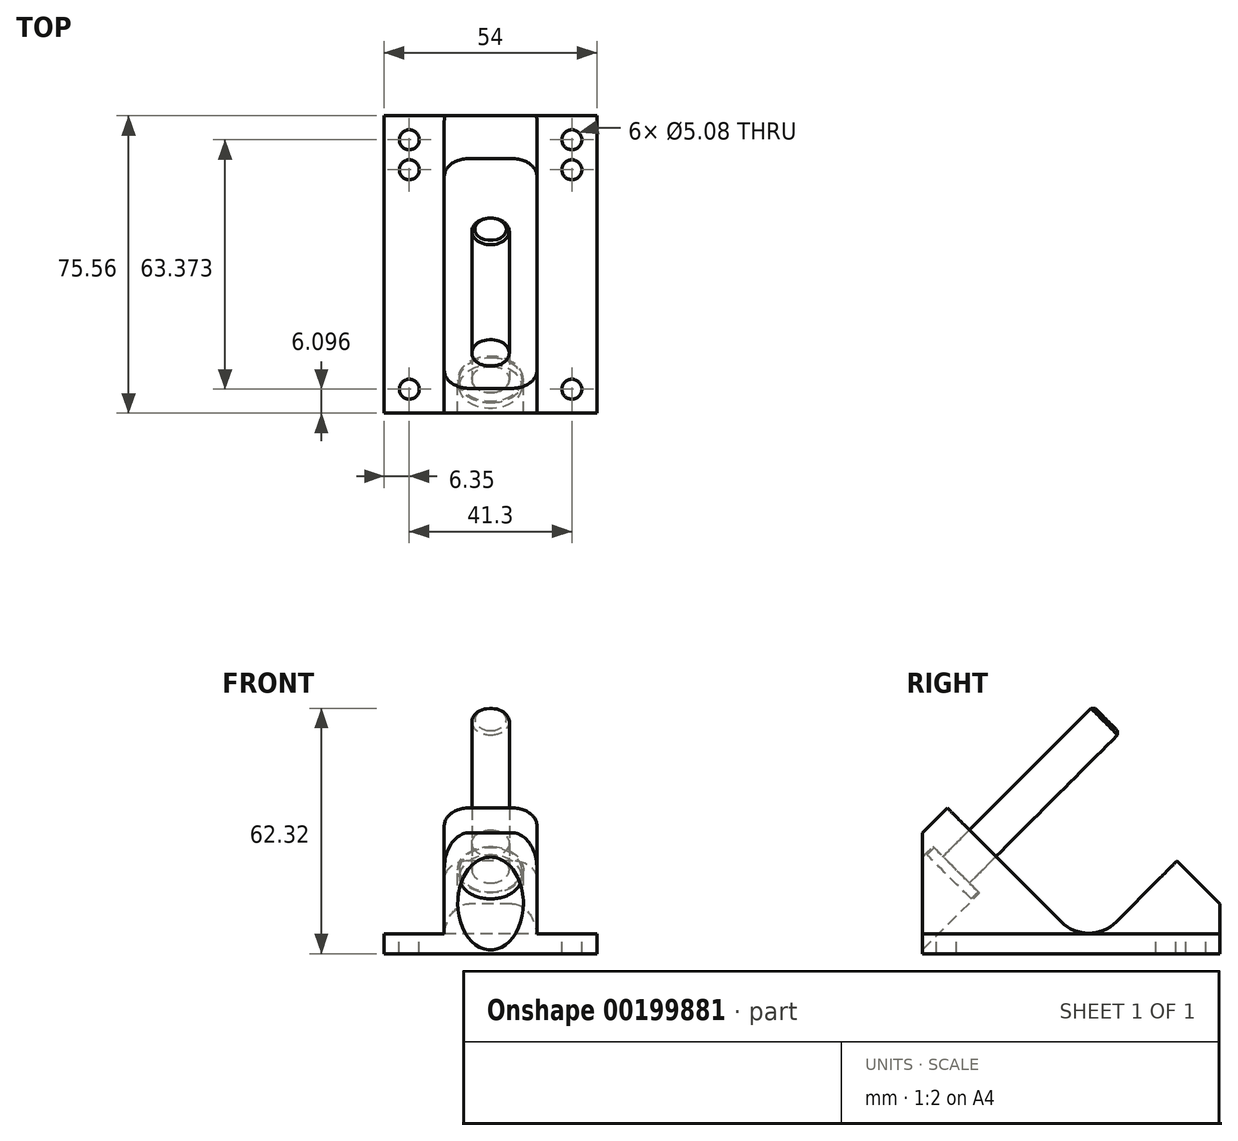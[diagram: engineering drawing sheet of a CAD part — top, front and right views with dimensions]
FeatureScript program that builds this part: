
annotation { "Feature Type Name" : "Feature", "Feature Type Description" : "" }
export const myFeature = defineFeature(function(context is Context, id is Id, definition is map)
    precondition{}
    {
        {
            var Q0;
            Q0=qCreatedBy(makeId("Right.planeOp"),FACE);
            var sketch = newSketch(context, id + "F0", { "sketchPlane" : qUnion([Q0])});
            skLineSegment(sketch, "E0", {"start": v(0, 0) * mm, "end": v(0, 30.72) * mm});
            skLineSegment(sketch, "E1", {"start": v(0, 30.72) * mm, "end": v(6.32, 37.04) * mm});
            skLineSegment(sketch, "E2", {"start": v(6.32, 37.04) * mm, "end": v(42.25, 1.12) * mm});
            skLineSegment(sketch, "E3", {"start": v(42.25, 1.12) * mm, "end": v(64.7, 23.57) * mm});
            skLineSegment(sketch, "E4", {"start": v(64.7, 23.57) * mm, "end": v(75.57, 12.7) * mm});
            skLineSegment(sketch, "E5", {"start": v(75.57, 12.7) * mm, "end": v(75.57, 0) * mm});
            skLineSegment(sketch, "E6", {"start": v(75.57, 0) * mm, "end": v(0, 0) * mm});
            skLineSegment(sketch, "E7", {"start": v(15.3, 28.06) * mm, "end": v(28.77, 41.53) * mm, "construction": true});
            skLineSegment(sketch, "E8", {"start": v(28.77, 41.53) * mm, "end": v(55.72, 14.59) * mm, "construction": true});
            skLineSegment(sketch, "E9", {"start": v(55.72, 14.59) * mm, "end": v(64.7, 5.6) * mm, "construction": true});
            skLineSegment(sketch, "E10", {"start": v(64.7, 5.6) * mm, "end": v(70.08, 11) * mm, "construction": true});
            skLineSegment(sketch, "E11", {"start": v(70.08, 11) * mm, "end": v(61.1, 19.98) * mm, "construction": true});
            skLineSegment(sketch, "E12", {"start": v(28.77, 41.53) * mm, "end": v(15.3, 55) * mm, "construction": true});
            skCircle(sketch, "E13", {"center": v(15.3, 55) * mm, "radius": 4 * mm, "construction": true});
            skLineSegment(sketch, "E14", {"start": v(64.7, 5.6) * mm, "end": v(59.3, 0.22) * mm, "construction": true});
            skLineSegment(sketch, "E15", {"start": v(59.3, 0.22) * mm, "end": v(50.33, 9.2) * mm, "construction": true});
            skCircle(sketch, "E16", {"center": v(58.4, 11.9) * mm, "radius": 5.08 * mm, "construction": true});
            skSolve(sketch);
        }
        {
            var Q0;
            Q0 = qSketchRegion(id + "F0", true);
            extrude(context, id + "F1", {"entities" : qUnion([Q0]), "depth" : 27 * mm});
        }
        {
            var Q0;
            Q0=makeQuery(id+"F1.opExtrude","SWEPT_EDGE",EDGE,{"disambiguationData":[OSD([sQuery(id+"F0.wireOp",EDGE,"E2"),sQuery(id+"F0.wireOp",EDGE,"E3")])]});
            fillet(context, id + "F2", {"entities" : qUnion([Q0]), "radius" : 9.9 * mm, "tangentPropagation" : true, "allowEdgeOverflow" : false});
        }
        {
            var Q0;
            Q0=makeQuery(id+"F1.opExtrude","CAP_FACE",FACE,{"disambiguationData":[OSD([sQuery(id+"F0.wireOp",EDGE,"E0"),sQuery(id+"F0.wireOp",EDGE,"E1"),sQuery(id+"F0.wireOp",EDGE,"E2"),sQuery(id+"F0.wireOp",EDGE,"E3"),sQuery(id+"F0.wireOp",EDGE,"E4"),sQuery(id+"F0.wireOp",EDGE,"E5"),sQuery(id+"F0.wireOp",EDGE,"E6")])],"isStart":false});
            var sketch = newSketch(context, id + "F3", { "sketchPlane" : qUnion([Q0])});
            skLineSegment(sketch, "E17.bottom", {"start": v(0, 5.08) * mm, "end": v(75.57, 5.08) * mm});
            skLineSegment(sketch, "E17.top", {"start": v(0, 37.04) * mm, "end": v(75.57, 37.04) * mm});
            skLineSegment(sketch, "E17.left", {"start": v(0, 5.08) * mm, "end": v(0, 37.04) * mm});
            skLineSegment(sketch, "E17.right", {"start": v(75.57, 5.08) * mm, "end": v(75.57, 37.04) * mm});
            skSolve(sketch);
        }
        {
            var Q0;
            Q0 = qSketchRegion(id + "F3", true);
            extrude(context, id + "F4", {"entities" : qUnion([Q0]), "operationType" : NewBodyOperationType.REMOVE, "oppositeDirection" : true, "depth" : 15.24 * mm});
        }
        {
            var Q0;
            Q0=makeQuery(id+"F4.boolean.opBoolean","COPY",FACE,{"derivedFrom":makeQuery(id+"F4.opExtrude","SWEPT_FACE",FACE,{"disambiguationData":[OSD([sQuery(id+"F3.wireOp",EDGE,"E17.bottom")])]})});
            var sketch = newSketch(context, id + "F5", { "sketchPlane" : qUnion([Q0])});
            skLineSegment(sketch, "E18", {"start": v(20.65, 69.47) * mm, "end": v(20.65, 61.85) * mm, "construction": true});
            skLineSegment(sketch, "E19", {"start": v(20.65, 61.85) * mm, "end": v(20.65, 6.1) * mm, "construction": true});
            skCircle(sketch, "E20", {"center": v(20.65, 69.47) * mm, "radius": 2.54 * mm});
            skCircle(sketch, "E21", {"center": v(20.65, 61.85) * mm, "radius": 2.54 * mm});
            skCircle(sketch, "E22", {"center": v(20.65, 6.1) * mm, "radius": 2.54 * mm});
            skSolve(sketch);
        }
        {
            var Q0;
            Q0 = qSketchRegion(id + "F5", true);
            extrude(context, id + "F6", {"entities" : qUnion([Q0]), "operationType" : NewBodyOperationType.REMOVE, "endBound" : BoundingType.THROUGH_ALL, "oppositeDirection" : true, "depth" : 25.4 * mm});
        }
        {
            var Q0;
            Q0=makeQuery(id+"F1.opExtrude","SWEPT_BODY",BODY,{"disambiguationData":[OSD([sQuery(id+"F0.wireOp",EDGE,"E0"),sQuery(id+"F0.wireOp",EDGE,"E1"),sQuery(id+"F0.wireOp",EDGE,"E2"),sQuery(id+"F0.wireOp",EDGE,"E3"),sQuery(id+"F0.wireOp",EDGE,"E4"),sQuery(id+"F0.wireOp",EDGE,"E5"),sQuery(id+"F0.wireOp",EDGE,"E6")])]});
            var Q1;
            Q1=makeQuery(id+"F1.opExtrude","CAP_FACE",FACE,{"disambiguationData":[OSD([sQuery(id+"F0.wireOp",EDGE,"E0"),sQuery(id+"F0.wireOp",EDGE,"E1"),sQuery(id+"F0.wireOp",EDGE,"E2"),sQuery(id+"F0.wireOp",EDGE,"E3"),sQuery(id+"F0.wireOp",EDGE,"E4"),sQuery(id+"F0.wireOp",EDGE,"E5"),sQuery(id+"F0.wireOp",EDGE,"E6")])],"isStart":true});
            mirror(context, id + "F7", {"operationType" : NewBodyOperationType.ADD, "entities" : qUnion([Q0]), "mirrorPlane" : qUnion([Q1])});
        }
        {
            var Q0;
            Q0=makeQuery(id+"F7.opPattern","COPY",EDGE,{"derivedFrom":makeQuery(id+"F4.boolean.opBoolean","INTERSECT",EDGE,{"derivedFrom":[makeQuery(id+"F1.opExtrude","SWEPT_FACE",FACE,{"disambiguationData":[OSD([sQuery(id+"F0.wireOp",EDGE,"E1")])]}),makeQuery(id+"F4.opExtrude","CAP_FACE",FACE,{"disambiguationData":[OSD([sQuery(id+"F3.wireOp",EDGE,"E17.bottom"),sQuery(id+"F3.wireOp",EDGE,"E17.top"),sQuery(id+"F3.wireOp",EDGE,"E17.left"),sQuery(id+"F3.wireOp",EDGE,"E17.right")])],"isStart":false})]}),"instanceName":"1"});
            var Q1;
            Q1=makeQuery(id+"F4.boolean.opBoolean","INTERSECT",EDGE,{"derivedFrom":[makeQuery(id+"F1.opExtrude","SWEPT_FACE",FACE,{"disambiguationData":[OSD([sQuery(id+"F0.wireOp",EDGE,"E1")])]}),makeQuery(id+"F4.opExtrude","CAP_FACE",FACE,{"disambiguationData":[OSD([sQuery(id+"F3.wireOp",EDGE,"E17.bottom"),sQuery(id+"F3.wireOp",EDGE,"E17.top"),sQuery(id+"F3.wireOp",EDGE,"E17.left"),sQuery(id+"F3.wireOp",EDGE,"E17.right")])],"isStart":false})]});
            var Q2;
            Q2=makeQuery(id+"F7.opPattern","COPY",EDGE,{"derivedFrom":makeQuery(id+"F4.boolean.opBoolean","INTERSECT",EDGE,{"derivedFrom":[makeQuery(id+"F1.opExtrude","SWEPT_FACE",FACE,{"disambiguationData":[OSD([sQuery(id+"F0.wireOp",EDGE,"E4")])]}),makeQuery(id+"F4.opExtrude","CAP_FACE",FACE,{"disambiguationData":[OSD([sQuery(id+"F3.wireOp",EDGE,"E17.bottom"),sQuery(id+"F3.wireOp",EDGE,"E17.top"),sQuery(id+"F3.wireOp",EDGE,"E17.left"),sQuery(id+"F3.wireOp",EDGE,"E17.right")])],"isStart":false})]}),"instanceName":"1"});
            var Q3;
            Q3=makeQuery(id+"F4.boolean.opBoolean","INTERSECT",EDGE,{"derivedFrom":[makeQuery(id+"F1.opExtrude","SWEPT_FACE",FACE,{"disambiguationData":[OSD([sQuery(id+"F0.wireOp",EDGE,"E4")])]}),makeQuery(id+"F4.opExtrude","CAP_FACE",FACE,{"disambiguationData":[OSD([sQuery(id+"F3.wireOp",EDGE,"E17.bottom"),sQuery(id+"F3.wireOp",EDGE,"E17.top"),sQuery(id+"F3.wireOp",EDGE,"E17.left"),sQuery(id+"F3.wireOp",EDGE,"E17.right")])],"isStart":false})]});
            fillet(context, id + "F8", {"entities" : qUnion([Q0, Q1, Q2, Q3]), "radius" : 6.35 * mm, "tangentPropagation" : true, "allowEdgeOverflow" : false});
        }
        {
            var Q0;
            Q0=qCreatedBy(makeId("Right.planeOp"),FACE);
            var sketch = newSketch(context, id + "F9", { "sketchPlane" : qUnion([Q0])});
            skLineSegment(sketch, "E23.0", {"start": v(15.3, 28.06) * mm, "end": v(28.77, 41.53) * mm, "construction": true});
            skLineSegment(sketch, "E23.1", {"start": v(6.32, 37.04) * mm, "end": v(42.25, 1.12) * mm, "construction": true});
            skLineSegment(sketch, "E24", {"start": v(15.3, 28.06) * mm, "end": v(11.94, 31.43) * mm});
            skLineSegment(sketch, "E25", {"start": v(11.94, 31.43) * mm, "end": v(5.2, 24.7) * mm});
            skLineSegment(sketch, "E26", {"start": v(5.2, 24.7) * mm, "end": v(2.67, 27.22) * mm});
            skLineSegment(sketch, "E27", {"start": v(2.67, 27.22) * mm, "end": v(-12.28, 12.28) * mm});
            skLineSegment(sketch, "E28", {"start": v(-12.28, 12.28) * mm, "end": v(-6.38, 6.38) * mm});
            skLineSegment(sketch, "E29", {"start": v(-6.38, 6.38) * mm, "end": v(15.3, 28.06) * mm});
            skLineSegment(sketch, "E30", {"start": v(-6.38, 6.38) * mm, "end": v(0, 0) * mm, "construction": true});
            skSolve(sketch);
        }
        {
            var Q0;
            Q0 = qSketchRegion(id + "F9", true);
            var Q1;
            Q1=sQuery(id+"F9.wireOp",EDGE,"E23.0");
            revolve(context, id + "F10", {"operationType" : NewBodyOperationType.REMOVE, "entities" : qUnion([Q0]), "axis" : qUnion([Q1]), "revolveType" : RevolveType.FULL, "oppositeDirection" : true});
        }
        {
            var Q0;
            Q0=qCreatedBy(makeId("Right.planeOp"),FACE);
            var sketch = newSketch(context, id + "F11", { "sketchPlane" : qUnion([Q0])});
            skLineSegment(sketch, "E31.1", {"start": v(5.2, 24.7) * mm, "end": v(2.96, 26.94) * mm});
            skLineSegment(sketch, "E31.2", {"start": v(11.94, 31.43) * mm, "end": v(5.2, 24.7) * mm});
            skLineSegment(sketch, "E32", {"start": v(2.96, 26.94) * mm, "end": v(1.16, 25.14) * mm});
            skPoint(sketch, "E31.0.end.orphan", {"position": v(-12.28, 12.28) * mm});
            skPoint(sketch, "E31.0.start.orphan", {"position": v(2.67, 27.22) * mm});
            skLineSegment(sketch, "E33", {"start": v(1.16, 25.14) * mm, "end": v(6.77, 19.53) * mm});
            skLineSegment(sketch, "E34", {"start": v(6.77, 19.53) * mm, "end": v(46.74, 59.5) * mm});
            skLineSegment(sketch, "E35", {"start": v(46.74, 59.5) * mm, "end": v(43.37, 62.86) * mm});
            skLineSegment(sketch, "E36", {"start": v(43.37, 62.86) * mm, "end": v(11.94, 31.43) * mm});
            skSolve(sketch);
        }
        {
            var Q0;
            Q0 = qSketchRegion(id + "F11", true);
            var Q1;
            Q1=sQuery(id+"F11.wireOp",EDGE,"E34");
            revolve(context, id + "F12", {"entities" : qUnion([Q0]), "axis" : qUnion([Q1]), "revolveType" : RevolveType.FULL});
        }
        {
            var Q0;
            Q0=makeQuery(id+"F12.opRevolve","SWEPT_EDGE",EDGE,{"disambiguationData":[OSD([sQuery(id+"F11.wireOp",EDGE,"E35"),sQuery(id+"F11.wireOp",EDGE,"E36")])]});
            chamfer(context, id + "F13", {"entities" : qUnion([Q0]), "width" : 0.76 * mm, "tangentPropagation" : true});
        }
    });
